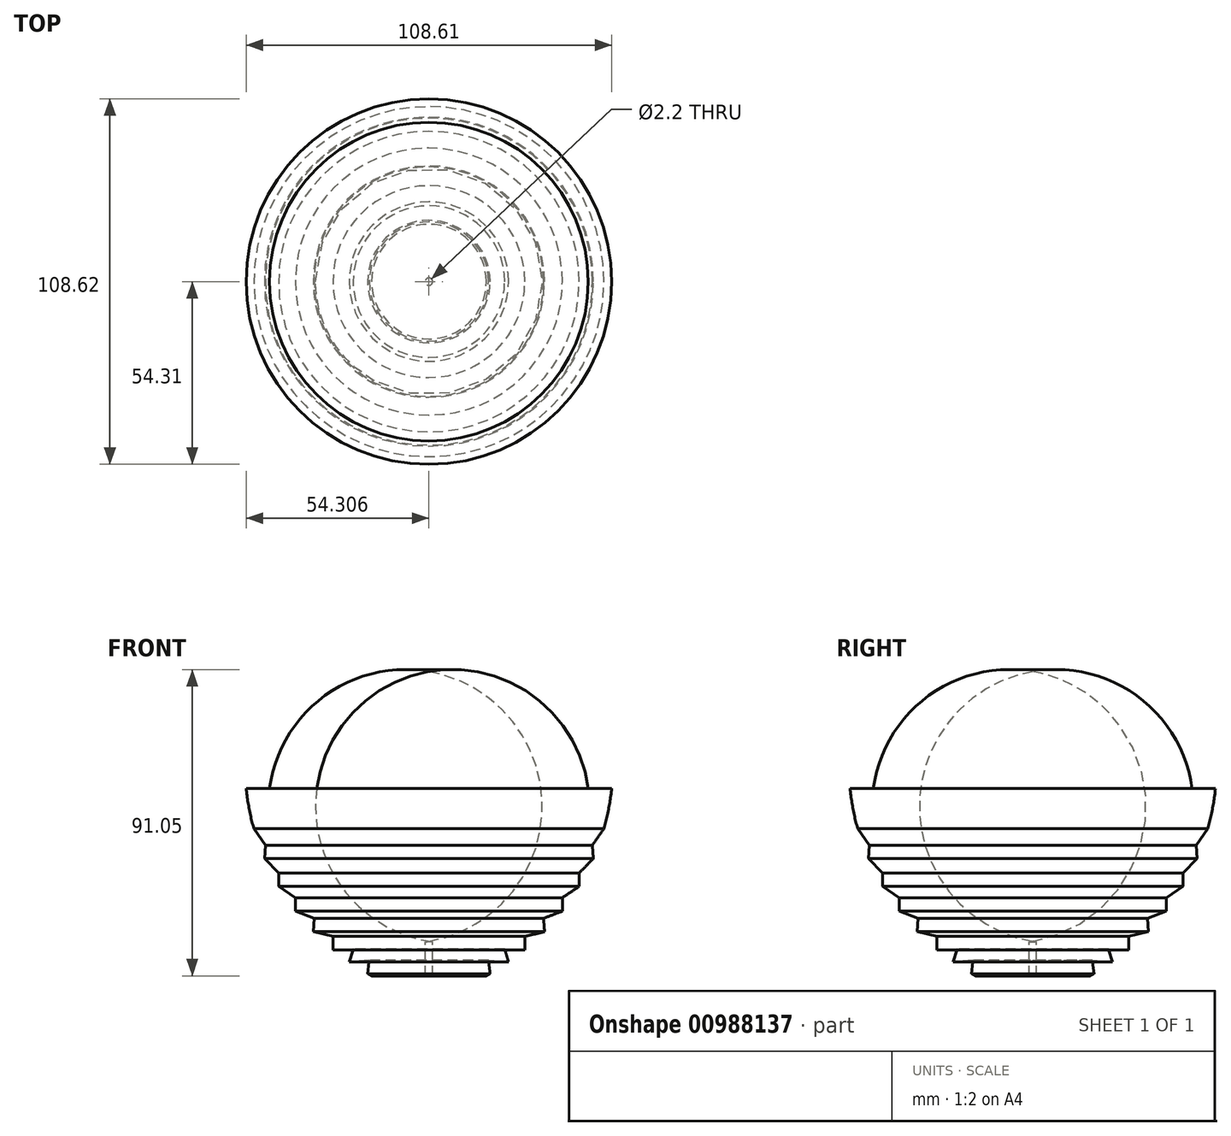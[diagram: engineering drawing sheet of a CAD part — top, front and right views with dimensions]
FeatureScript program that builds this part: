
annotation { "Feature Type Name" : "Feature", "Feature Type Description" : "" }
export const myFeature = defineFeature(function(context is Context, id is Id, definition is map)
    precondition{}
    {
        {
            var Q0;
            Q0=qCreatedBy(makeId("Front.planeOp"),FACE);
            var sketch = newSketch(context, id + "F0", { "sketchPlane" : qUnion([Q0])});
            skLineSegment(sketch, "E0", {"start": v(25.78, 45.62) * mm, "end": v(18.84, 45.62) * mm});
            skArc(sketch, "E1", {"start": v(-27.42, 0) * mm, "mid": v(7.07, 11.29) * mm, "end": v(18.84, 45.62) * mm});
            skLineSegment(sketch, "E2", {"start": v(-27.42, 0) * mm, "end": v(-27.42, -10.08) * mm});
            skLineSegment(sketch, "E3", {"start": v(-27.42, -10.08) * mm, "end": v(-11.48, -10.08) * mm});
            skArc(sketch, "E4", {"start": v(-11.48, -10.08) * mm, "mid": v(14.03, 13.17) * mm, "end": v(25.78, 45.62) * mm});
            skLineSegment(sketch, "E5", {"start": v(23.5, 33.7) * mm, "end": v(20.07, 28.77) * mm});
            skLineSegment(sketch, "E6", {"start": v(20.07, 28.77) * mm, "end": v(20.34, 24.78) * mm});
            skLineSegment(sketch, "E7", {"start": v(20.34, 24.78) * mm, "end": v(16.14, 20.5) * mm});
            skLineSegment(sketch, "E8", {"start": v(16.14, 20.5) * mm, "end": v(16.14, 16.5) * mm});
            skLineSegment(sketch, "E9", {"start": v(16.14, 16.5) * mm, "end": v(11.15, 13.17) * mm});
            skPoint(sketch, "E9.endSnap0", {"position": v(14.03, 13.17) * mm});
            skLineSegment(sketch, "E10", {"start": v(11.15, 13.17) * mm, "end": v(11.15, 9.17) * mm});
            skLineSegment(sketch, "E11", {"start": v(11.15, 9.17) * mm, "end": v(5.55, 7.03) * mm});
            skLineSegment(sketch, "E12", {"start": v(5.55, 7.03) * mm, "end": v(5.84, 3.04) * mm});
            skLineSegment(sketch, "E13", {"start": v(5.84, 3.04) * mm, "end": v(0, 1.66) * mm});
            skLineSegment(sketch, "E14", {"start": v(0, 1.66) * mm, "end": v(0, -2.34) * mm});
            skLineSegment(sketch, "E15", {"start": v(0, -2.34) * mm, "end": v(-6, -2.17) * mm});
            skLineSegment(sketch, "E16", {"start": v(-6, -2.17) * mm, "end": v(-4.84, -6) * mm});
            skLineSegment(sketch, "E17", {"start": v(-4.84, -6) * mm, "end": v(-10.81, -5.47) * mm});
            skLineSegment(sketch, "E18", {"start": v(-10.81, -5.47) * mm, "end": v(-10.33, -9.44) * mm});
            skSolve(sketch);
        }
        {
            var Q0;
            Q0=qCreatedBy(makeId("Top.planeOp"),FACE);
            var sketch = newSketch(context, id + "F1", { "sketchPlane" : qUnion([Q0])});
            skCircle(sketch, "E19", {"center": v(-28.52, 0) * mm, "radius": 52.72 * mm});
            skCircle(sketch, "E20", {"center": v(-28.52, 0) * mm, "radius": 0.4 * mm});
            skSolve(sketch);
        }
        {
            var Q0;
            Q0=makeQuery(id+"F0.imprint","IMPRINT",FACE,{"disambiguationData":[TD([[makeQuery(id+"F0.imprint","IMPRINT",EDGE,{"derivedFrom":sQuery(id+"F0.wireOp",EDGE,"E0")}),1.0]])]});
            var Q1;
            Q1=sQuery(id+"F1.wireOp",EDGE,"E19");
            sweep(context, id + "F2", {"profiles" : qUnion([Q0]), "path" : qUnion([Q1])});
        }
    });
